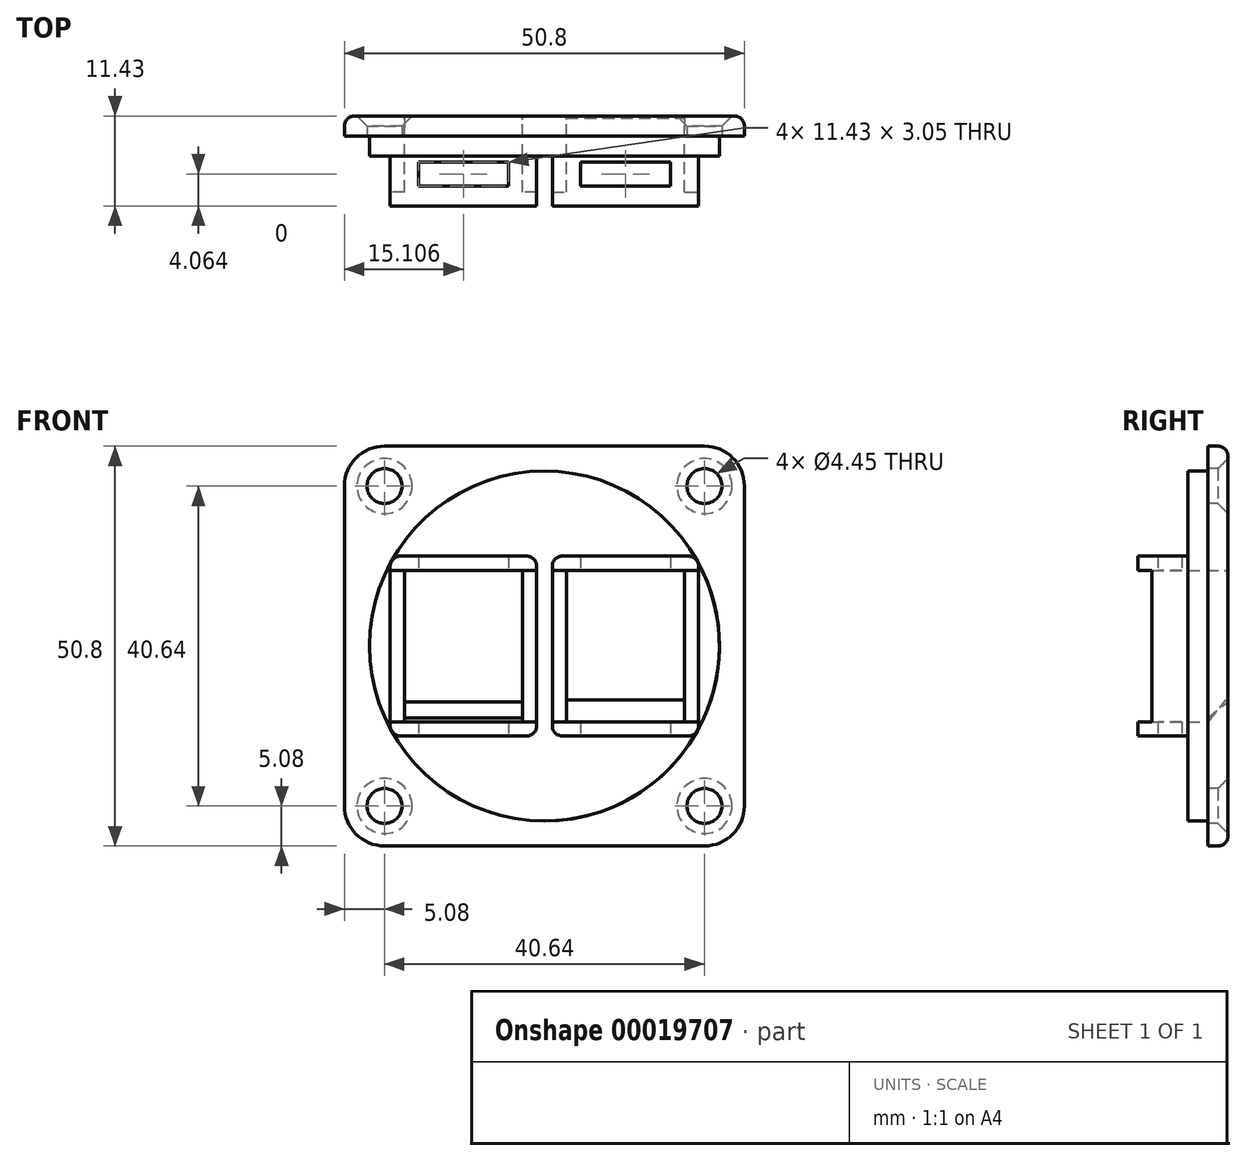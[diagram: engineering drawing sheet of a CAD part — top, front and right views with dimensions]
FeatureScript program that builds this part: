
annotation { "Feature Type Name" : "Feature", "Feature Type Description" : "" }
export const myFeature = defineFeature(function(context is Context, id is Id, definition is map)
    precondition{}
    {
        {
            var Q0;
            Q0=qCreatedBy(makeId("Front.planeOp"),FACE);
            var sketch = newSketch(context, id + "F0", { "sketchPlane" : qUnion([Q0])});
            skCircle(sketch, "E0", {"center": v(0, 0) * mm, "radius": 22.22 * mm});
            skSolve(sketch);
        }
        {
            var Q0;
            Q0 = qSketchRegion(id + "F0", true);
            extrude(context, id + "F1", {"entities" : qUnion([Q0]), "depth" : 2.54 * mm});
        }
        {
            var Q0;
            Q0=makeQuery(id+"F1.opExtrude","CAP_FACE",FACE,{"disambiguationData":[OSD([sQuery(id+"F0.wireOp",EDGE,"E0")])],"isStart":true});
            var sketch = newSketch(context, id + "F2", { "sketchPlane" : qUnion([Q0])});
            skLineSegment(sketch, "E1.rect.bottom", {"start": v(20.32, -25.4) * mm, "end": v(-20.32, -25.4) * mm});
            skLineSegment(sketch, "E1.rect.top", {"start": v(20.32, 25.4) * mm, "end": v(-20.32, 25.4) * mm});
            skLineSegment(sketch, "E1.rect.left", {"start": v(25.4, -20.32) * mm, "end": v(25.4, 20.32) * mm});
            skLineSegment(sketch, "E1.rect.right", {"start": v(-25.4, -20.32) * mm, "end": v(-25.4, 20.32) * mm});
            skPoint(sketch, "E1.rect.middle", {"position": v(0, 0) * mm});
            skPoint(sketch, "E2.visualSharp", {"position": v(-25.4, 25.4) * mm});
            skArc(sketch, "E2.filletArc", {"start": v(-20.32, 25.4) * mm, "mid": v(-23.91, 23.91) * mm, "end": v(-25.4, 20.32) * mm});
            skPoint(sketch, "E3.visualSharp", {"position": v(25.4, 25.4) * mm});
            skArc(sketch, "E3.filletArc", {"start": v(25.4, 20.32) * mm, "mid": v(23.91, 23.91) * mm, "end": v(20.32, 25.4) * mm});
            skPoint(sketch, "E4.visualSharp", {"position": v(25.4, -25.4) * mm});
            skArc(sketch, "E4.filletArc", {"start": v(20.32, -25.4) * mm, "mid": v(23.91, -23.91) * mm, "end": v(25.4, -20.32) * mm});
            skPoint(sketch, "E5.visualSharp", {"position": v(-25.4, -25.4) * mm});
            skArc(sketch, "E5.filletArc", {"start": v(-25.4, -20.32) * mm, "mid": v(-23.91, -23.91) * mm, "end": v(-20.32, -25.4) * mm});
            skCircle(sketch, "E6", {"center": v(-20.32, 20.32) * mm, "radius": 2.22 * mm});
            skCircle(sketch, "E7", {"center": v(20.32, 20.32) * mm, "radius": 2.22 * mm});
            skCircle(sketch, "E8", {"center": v(20.32, -20.32) * mm, "radius": 2.22 * mm});
            skCircle(sketch, "E9", {"center": v(-20.32, -20.32) * mm, "radius": 2.22 * mm});
            skSolve(sketch);
        }
        {
            var Q0;
            Q0 = qSketchRegion(id + "F2", true);
            extrude(context, id + "F3", {"entities" : qUnion([Q0]), "operationType" : NewBodyOperationType.ADD, "depth" : 2.54 * mm});
        }
        {
            var Q0;
            Q0=makeQuery(id+"F3.opExtrude","CAP_FACE",FACE,{"disambiguationData":[OSD([sQuery(id+"F2.wireOp",EDGE,"E1.rect.bottom"),sQuery(id+"F2.wireOp",EDGE,"E1.rect.top"),sQuery(id+"F2.wireOp",EDGE,"E1.rect.left"),sQuery(id+"F2.wireOp",EDGE,"E1.rect.right"),sQuery(id+"F2.wireOp",EDGE,"E2.filletArc"),sQuery(id+"F2.wireOp",EDGE,"E3.filletArc"),sQuery(id+"F2.wireOp",EDGE,"E4.filletArc"),sQuery(id+"F2.wireOp",EDGE,"E5.filletArc"),sQuery(id+"F2.wireOp",EDGE,"E6"),sQuery(id+"F2.wireOp",EDGE,"E7"),sQuery(id+"F2.wireOp",EDGE,"E8"),sQuery(id+"F2.wireOp",EDGE,"E9")])],"isStart":false});
            var sketch = newSketch(context, id + "F4", { "sketchPlane" : qUnion([Q0])});
            skLineSegment(sketch, "E10.rect.bottom", {"start": v(-2.8, -9.63) * mm, "end": v(-17.8, -9.62) * mm});
            skLineSegment(sketch, "E10.rect.top", {"start": v(-2.8, 9.62) * mm, "end": v(-17.8, 9.63) * mm});
            skLineSegment(sketch, "E10.rect.left", {"start": v(-2.8, -9.63) * mm, "end": v(-2.8, 9.62) * mm});
            skLineSegment(sketch, "E10.rect.right", {"start": v(-17.8, -9.62) * mm, "end": v(-17.8, 9.63) * mm});
            skPoint(sketch, "E10.rect.middle", {"position": v(-10.3, 0) * mm});
            skLineSegment(sketch, "E11", {"start": v(0, 25.4) * mm, "end": v(0, -25.4) * mm, "construction": true});
            skLineSegment(sketch, "E12.MirrorCS", {"start": v(2.8, -9.63) * mm, "end": v(17.8, -9.63) * mm});
            skLineSegment(sketch, "E13.MirrorCS", {"start": v(2.8, -9.62) * mm, "end": v(2.8, 9.62) * mm});
            skLineSegment(sketch, "E14.MirrorCS", {"start": v(2.8, 9.62) * mm, "end": v(17.8, 9.62) * mm});
            skLineSegment(sketch, "E15.MirrorCS", {"start": v(17.8, -9.62) * mm, "end": v(17.8, 9.63) * mm});
            skSolve(sketch);
        }
        {
            var Q0;
            Q0 = qSketchRegion(id + "F4", true);
            extrude(context, id + "F5", {"entities" : qUnion([Q0]), "operationType" : NewBodyOperationType.REMOVE, "endBound" : BoundingType.THROUGH_ALL, "oppositeDirection" : true, "depth" : 25.4 * mm});
        }
        {
            var Q0;
            Q0=makeQuery(id+"F1.opExtrude","CAP_FACE",FACE,{"disambiguationData":[OSD([sQuery(id+"F0.wireOp",EDGE,"E0")])],"isStart":false});
            var sketch = newSketch(context, id + "F6", { "sketchPlane" : qUnion([Q0])});
            skLineSegment(sketch, "E16.0", {"start": v(18.32, 11.42) * mm, "end": v(2.26, 11.42) * mm});
            skLineSegment(sketch, "E16.1", {"start": v(19.6, 10.15) * mm, "end": v(19.6, -10.16) * mm});
            skLineSegment(sketch, "E16.2", {"start": v(18.32, -11.43) * mm, "end": v(2.26, -11.43) * mm});
            skLineSegment(sketch, "E16.3", {"start": v(1, 10.15) * mm, "end": v(1, -10.16) * mm});
            skLineSegment(sketch, "E17.0", {"start": v(17.8, 9.62) * mm, "end": v(2.8, 9.62) * mm});
            skLineSegment(sketch, "E17.1", {"start": v(17.8, 9.62) * mm, "end": v(17.8, -9.62) * mm});
            skLineSegment(sketch, "E17.2", {"start": v(17.8, -9.63) * mm, "end": v(2.8, -9.63) * mm});
            skLineSegment(sketch, "E17.3", {"start": v(2.8, 9.62) * mm, "end": v(2.8, -9.62) * mm});
            skPoint(sketch, "E18.visualSharp", {"position": v(1, 11.42) * mm});
            skArc(sketch, "E18.filletArc", {"start": v(2.26, 11.42) * mm, "mid": v(1.37, 11.05) * mm, "end": v(1, 10.15) * mm});
            skPoint(sketch, "E19.visualSharp", {"position": v(19.6, 11.42) * mm});
            skArc(sketch, "E19.filletArc", {"start": v(19.6, 10.15) * mm, "mid": v(19.22, 11.05) * mm, "end": v(18.32, 11.42) * mm});
            skPoint(sketch, "E20.visualSharp", {"position": v(19.6, -11.43) * mm});
            skArc(sketch, "E20.filletArc", {"start": v(18.32, -11.43) * mm, "mid": v(19.22, -11.05) * mm, "end": v(19.6, -10.16) * mm});
            skPoint(sketch, "E21.visualSharp", {"position": v(1, -11.43) * mm});
            skArc(sketch, "E21.filletArc", {"start": v(1, -10.16) * mm, "mid": v(1.37, -11.05) * mm, "end": v(2.26, -11.43) * mm});
            skLineSegment(sketch, "E22", {"start": v(0, 22.22) * mm, "end": v(0, -22.22) * mm, "construction": true});
            skLineSegment(sketch, "E23.MirrorCS", {"start": v(-18.32, 11.42) * mm, "end": v(-2.26, 11.42) * mm});
            skArc(sketch, "E24.MirrorCS", {"start": v(-2.26, 11.42) * mm, "mid": v(-1.37, 11.05) * mm, "end": v(-1, 10.15) * mm});
            skLineSegment(sketch, "E25.MirrorCS", {"start": v(-1, 10.15) * mm, "end": v(-1, -10.16) * mm});
            skArc(sketch, "E26.MirrorCS", {"start": v(-1, -10.16) * mm, "mid": v(-1.37, -11.05) * mm, "end": v(-2.26, -11.43) * mm});
            skLineSegment(sketch, "E27.MirrorCS", {"start": v(-18.32, -11.43) * mm, "end": v(-2.26, -11.43) * mm});
            skArc(sketch, "E28.MirrorCS", {"start": v(-18.32, -11.43) * mm, "mid": v(-19.22, -11.05) * mm, "end": v(-19.6, -10.16) * mm});
            skLineSegment(sketch, "E29.MirrorCS", {"start": v(-19.6, 10.15) * mm, "end": v(-19.6, -10.16) * mm});
            skArc(sketch, "E30.MirrorCS", {"start": v(-19.6, 10.15) * mm, "mid": v(-19.22, 11.05) * mm, "end": v(-18.32, 11.42) * mm});
            skLineSegment(sketch, "E31.MirrorCS", {"start": v(-17.8, 9.62) * mm, "end": v(-2.8, 9.62) * mm});
            skLineSegment(sketch, "E32.MirrorCS", {"start": v(-17.8, 9.62) * mm, "end": v(-17.8, -9.63) * mm});
            skLineSegment(sketch, "E33.MirrorCS", {"start": v(-17.8, -9.63) * mm, "end": v(-2.8, -9.63) * mm});
            skLineSegment(sketch, "E34.MirrorCS", {"start": v(-2.8, 9.62) * mm, "end": v(-2.8, -9.62) * mm});
            skSolve(sketch);
        }
        {
            var Q0;
            Q0 = qSketchRegion(id + "F6", true);
            extrude(context, id + "F7", {"entities" : qUnion([Q0]), "operationType" : NewBodyOperationType.ADD, "depth" : 6.35 * mm});
        }
        {
            var Q0;
            Q0=makeQuery(id+"F7.opExtrude","SWEPT_FACE",FACE,{"disambiguationData":[OSD([sQuery(id+"F6.wireOp",EDGE,"E16.2")])]});
            var sketch = newSketch(context, id + "F8", { "sketchPlane" : qUnion([Q0])});
            skLineSegment(sketch, "E35", {"start": v(10.3, 8.9) * mm, "end": v(10.3, 2.54) * mm, "construction": true});
            skLineSegment(sketch, "E36.rect.bottom", {"start": v(16, 3.3) * mm, "end": v(4.58, 3.3) * mm});
            skLineSegment(sketch, "E36.rect.top", {"start": v(16, 6.35) * mm, "end": v(4.58, 6.35) * mm});
            skLineSegment(sketch, "E36.rect.left", {"start": v(16, 3.3) * mm, "end": v(16, 6.35) * mm});
            skLineSegment(sketch, "E36.rect.right", {"start": v(4.58, 3.3) * mm, "end": v(4.58, 6.35) * mm});
            skPoint(sketch, "E36.rect.middle", {"position": v(10.3, 4.83) * mm});
            skLineSegment(sketch, "E37.MirrorCS", {"start": v(-16, 6.35) * mm, "end": v(-4.58, 6.35) * mm});
            skLineSegment(sketch, "E38.MirrorCS", {"start": v(-4.58, 3.3) * mm, "end": v(-4.58, 6.35) * mm});
            skLineSegment(sketch, "E39.MirrorCS", {"start": v(-16, 3.3) * mm, "end": v(-4.58, 3.3) * mm});
            skLineSegment(sketch, "E40.MirrorCS", {"start": v(-16, 3.3) * mm, "end": v(-16, 6.35) * mm});
            skSolve(sketch);
        }
        {
            var Q0;
            Q0 = qSketchRegion(id + "F8", true);
            extrude(context, id + "F9", {"entities" : qUnion([Q0]), "operationType" : NewBodyOperationType.REMOVE, "endBound" : BoundingType.THROUGH_ALL, "oppositeDirection" : true, "depth" : 25.4 * mm});
        }
        {
            var Q0;
            Q0=makeQuery(id+"F7.opExtrude","CAP_FACE",FACE,{"disambiguationData":[OSD([sQuery(id+"F6.wireOp",EDGE,"E16.0"),sQuery(id+"F6.wireOp",EDGE,"E16.1"),sQuery(id+"F6.wireOp",EDGE,"E16.2"),sQuery(id+"F6.wireOp",EDGE,"E16.3"),sQuery(id+"F6.wireOp",EDGE,"E17.0"),sQuery(id+"F6.wireOp",EDGE,"E17.1"),sQuery(id+"F6.wireOp",EDGE,"E17.2"),sQuery(id+"F6.wireOp",EDGE,"E17.3"),sQuery(id+"F6.wireOp",EDGE,"E18.filletArc"),sQuery(id+"F6.wireOp",EDGE,"E19.filletArc"),sQuery(id+"F6.wireOp",EDGE,"E20.filletArc"),sQuery(id+"F6.wireOp",EDGE,"E21.filletArc")])],"isStart":false});
            var sketch = newSketch(context, id + "F10", { "sketchPlane" : qUnion([Q0])});
            skLineSegment(sketch, "E41.bottom", {"start": v(1, 9.62) * mm, "end": v(19.6, 9.62) * mm});
            skLineSegment(sketch, "E41.top", {"start": v(1, -9.63) * mm, "end": v(19.6, -9.63) * mm});
            skLineSegment(sketch, "E41.left", {"start": v(1, 9.62) * mm, "end": v(1, -9.62) * mm});
            skLineSegment(sketch, "E41.right", {"start": v(19.6, 9.62) * mm, "end": v(19.6, -9.63) * mm});
            skLineSegment(sketch, "E42.MirrorCS", {"start": v(-1, 9.62) * mm, "end": v(-19.6, 9.62) * mm});
            skLineSegment(sketch, "E43.MirrorCS", {"start": v(-1, 9.62) * mm, "end": v(-1, -9.62) * mm});
            skLineSegment(sketch, "E44.MirrorCS", {"start": v(-1, -9.62) * mm, "end": v(-19.6, -9.63) * mm});
            skLineSegment(sketch, "E45.MirrorCS", {"start": v(-19.6, 9.62) * mm, "end": v(-19.6, -9.63) * mm});
            skSolve(sketch);
        }
        {
            var Q0;
            Q0 = qSketchRegion(id + "F10", true);
            extrude(context, id + "F11", {"entities" : qUnion([Q0]), "operationType" : NewBodyOperationType.REMOVE, "oppositeDirection" : true, "depth" : 1.78 * mm});
        }
        {
            var Q0;
            Q0=makeQuery(id+"F3.opExtrude","CAP_FACE",FACE,{"disambiguationData":[OSD([sQuery(id+"F2.wireOp",EDGE,"E1.rect.bottom"),sQuery(id+"F2.wireOp",EDGE,"E1.rect.top"),sQuery(id+"F2.wireOp",EDGE,"E1.rect.left"),sQuery(id+"F2.wireOp",EDGE,"E1.rect.right"),sQuery(id+"F2.wireOp",EDGE,"E2.filletArc"),sQuery(id+"F2.wireOp",EDGE,"E3.filletArc"),sQuery(id+"F2.wireOp",EDGE,"E4.filletArc"),sQuery(id+"F2.wireOp",EDGE,"E5.filletArc"),sQuery(id+"F2.wireOp",EDGE,"E6"),sQuery(id+"F2.wireOp",EDGE,"E7"),sQuery(id+"F2.wireOp",EDGE,"E8"),sQuery(id+"F2.wireOp",EDGE,"E9")])],"isStart":false});
            var sketch = newSketch(context, id + "F12", { "sketchPlane" : qUnion([Q0])});
            skLineSegment(sketch, "E46.bottom", {"start": v(-2.8, -9.63) * mm, "end": v(-17.8, -9.63) * mm});
            skLineSegment(sketch, "E46.top", {"start": v(-2.8, -6.88) * mm, "end": v(-17.8, -6.87) * mm});
            skLineSegment(sketch, "E46.left", {"start": v(-2.8, -9.63) * mm, "end": v(-2.8, -6.88) * mm});
            skLineSegment(sketch, "E46.right", {"start": v(-17.8, -9.63) * mm, "end": v(-17.8, -6.87) * mm});
            skLineSegment(sketch, "E47.MirrorCS", {"start": v(2.8, -6.88) * mm, "end": v(17.8, -6.88) * mm});
            skLineSegment(sketch, "E48.MirrorCS", {"start": v(17.8, -9.63) * mm, "end": v(17.8, -6.87) * mm});
            skLineSegment(sketch, "E49.MirrorCS", {"start": v(2.8, -9.63) * mm, "end": v(17.8, -9.62) * mm});
            skLineSegment(sketch, "E50.MirrorCS", {"start": v(2.8, -9.63) * mm, "end": v(2.8, -6.88) * mm});
            skSolve(sketch);
        }
        {
            var Q0;
            Q0 = qSketchRegion(id + "F12", true);
            extrude(context, id + "F13", {"entities" : qUnion([Q0]), "operationType" : NewBodyOperationType.ADD, "oppositeDirection" : true, "depth" : 2.54 * mm});
        }
        {
            var Q0;
            Q0=makeQuery(id+"F3.opExtrude","CAP_EDGE",EDGE,{"disambiguationData":[OSD([sQuery(id+"F2.wireOp",EDGE,"E6")])],"isStart":false});
            var Q1;
            Q1=makeQuery(id+"F3.opExtrude","CAP_EDGE",EDGE,{"disambiguationData":[OSD([sQuery(id+"F2.wireOp",EDGE,"E9")])],"isStart":false});
            var Q2;
            Q2=makeQuery(id+"F3.opExtrude","CAP_EDGE",EDGE,{"disambiguationData":[OSD([sQuery(id+"F2.wireOp",EDGE,"E8")])],"isStart":false});
            var Q3;
            Q3=makeQuery(id+"F3.opExtrude","CAP_EDGE",EDGE,{"disambiguationData":[OSD([sQuery(id+"F2.wireOp",EDGE,"E7")])],"isStart":false});
            chamfer(context, id + "F14", {"entities" : qUnion([Q0, Q1, Q2, Q3]), "width" : 1.27 * mm, "tangentPropagation" : true});
        }
        {
            var Q0;
            Q0=makeQuery(id+"F3.opExtrude","CAP_EDGE",EDGE,{"disambiguationData":[OSD([sQuery(id+"F2.wireOp",EDGE,"E1.rect.bottom")])],"isStart":false});
            fillet(context, id + "F15", {"entities" : qUnion([Q0]), "radius" : 1.27 * mm, "tangentPropagation" : true, "allowEdgeOverflow" : false});
        }
        {
            var Q0;
            Q0=makeQuery(id+"F13.opExtrude","CAP_EDGE",EDGE,{"disambiguationData":[OSD([sQuery(id+"F12.wireOp",EDGE,"E47.MirrorCS")])],"isStart":false});
            var Q1;
            Q1=makeQuery(id+"F13.opExtrude","CAP_EDGE",EDGE,{"disambiguationData":[OSD([sQuery(id+"F12.wireOp",EDGE,"E46.top")])],"isStart":false});
            chamfer(context, id + "F16", {"entities" : qUnion([Q0, Q1]), "chamferType" : ChamferType.TWO_OFFSETS, "width1" : 2.3 * mm, "oppositeDirection" : false, "width2" : 2.8 * mm, "tangentPropagation" : true});
        }
    });
